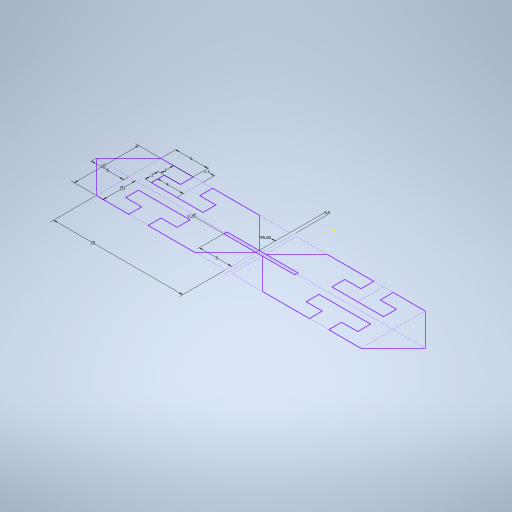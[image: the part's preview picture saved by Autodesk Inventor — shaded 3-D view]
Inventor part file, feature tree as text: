
AUTODESK INVENTOR PART (.ipt)
format: ipt  version: 2023 (Build 270158000, 158)  size: 267,264 bytes
history: native  units: in
note: dims shown in document units (in); Inventor stores cm internally (conversion verified against a paired STEP export)
features: sketch x1
ambient origin geometry x8: Origin, YZ Plane, XZ Plane, XY Plane, X Axis, Y Axis, Z Axis, Center Point
feature tree (1):
  sketch  "Sketch1"  dims[d0=0.7874in d1=0.3937in d2=0.1969in d3=0.1969in d4=0.1969in d5=0.0098in d6=0.0787in d7=0.0787in d8=0.1575in d9=0.0591in d10=0.1969in d11=0.0197in d12=45.0deg]
